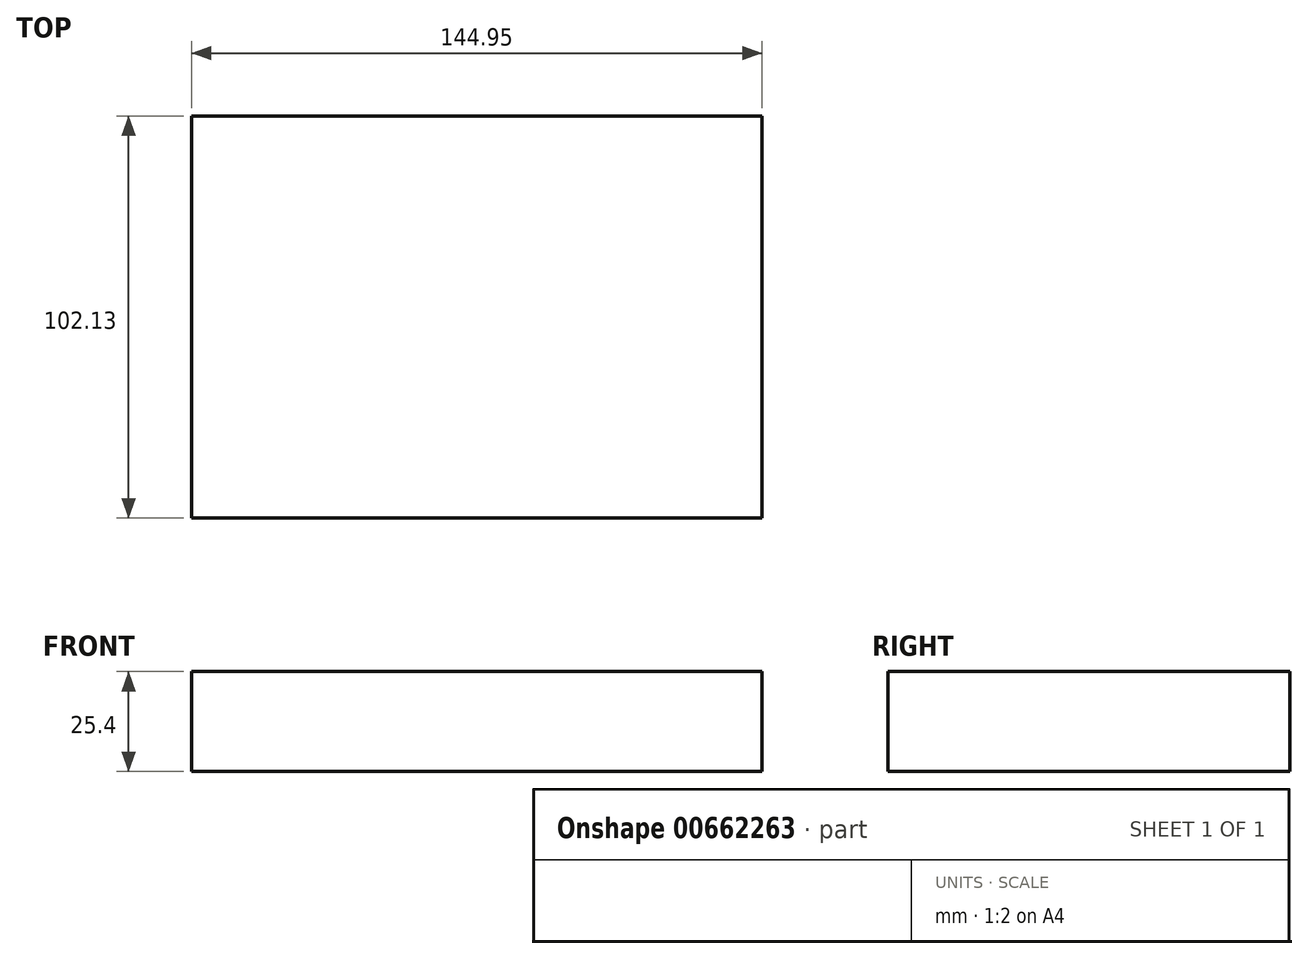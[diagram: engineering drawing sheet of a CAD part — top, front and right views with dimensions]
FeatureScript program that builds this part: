
annotation { "Feature Type Name" : "Feature", "Feature Type Description" : "" }
export const myFeature = defineFeature(function(context is Context, id is Id, definition is map)
    precondition{}
    {
        {
            var Q0;
            Q0=qCreatedBy(makeId("Top.planeOp"),FACE);
            var sketch = newSketch(context, id + "F0", { "sketchPlane" : qUnion([Q0])});
            skLineSegment(sketch, "E0.bottom", {"start": v(-129.7, 12.25) * mm, "end": v(15.25, 12.25) * mm});
            skLineSegment(sketch, "E0.top", {"start": v(-129.7, -89.88) * mm, "end": v(15.25, -89.88) * mm});
            skLineSegment(sketch, "E0.left", {"start": v(-129.7, 12.25) * mm, "end": v(-129.7, -89.88) * mm});
            skLineSegment(sketch, "E0.right", {"start": v(15.25, 12.25) * mm, "end": v(15.25, -89.88) * mm});
            skSolve(sketch);
        }
        {
            var Q0;
            Q0 = qSketchRegion(id + "F0", true);
            extrude(context, id + "F1", {"entities" : qUnion([Q0]), "depth" : 25.4 * mm, "offsetDistance" : 25.4 * mm});
        }
    });
